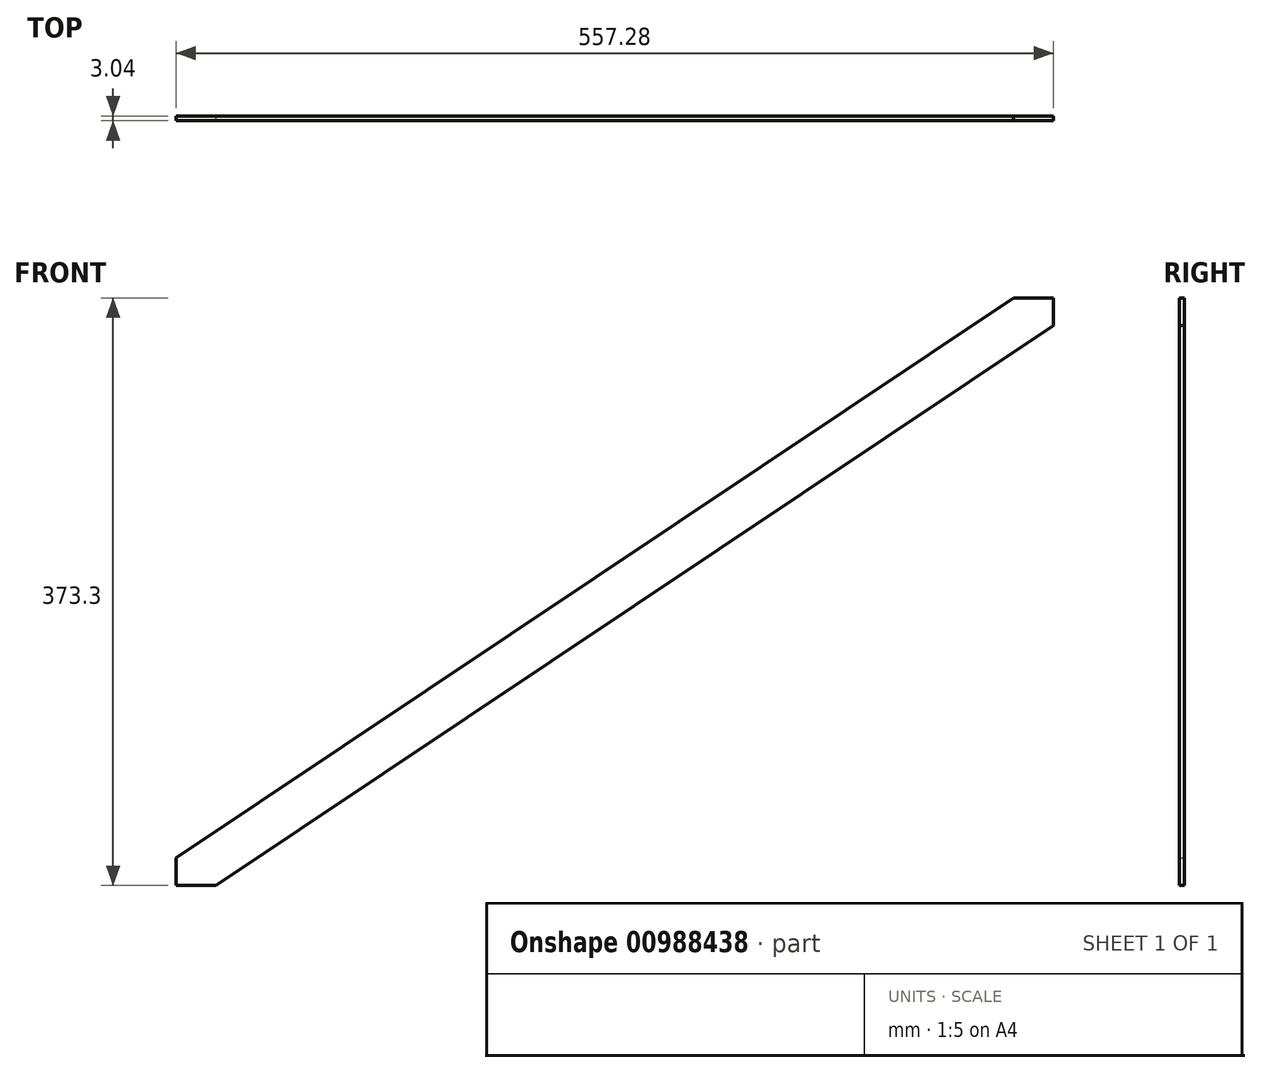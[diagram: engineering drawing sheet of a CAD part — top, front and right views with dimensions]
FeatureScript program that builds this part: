
annotation { "Feature Type Name" : "Feature", "Feature Type Description" : "" }
export const myFeature = defineFeature(function(context is Context, id is Id, definition is map)
    precondition{}
    {
        {
            var Q0;
            Q0=qCreatedBy(makeId("Front.planeOp"),FACE);
            var sketch = newSketch(context, id + "F0", { "sketchPlane" : qUnion([Q0])});
            skLineSegment(sketch, "E0.bottom", {"start": v(278.64, 186.65) * mm, "end": v(-278.64, 186.65) * mm, "construction": true});
            skLineSegment(sketch, "E0.top", {"start": v(278.64, -186.65) * mm, "end": v(-278.64, -186.65) * mm, "construction": true});
            skLineSegment(sketch, "E0.left", {"start": v(278.64, 186.65) * mm, "end": v(278.64, -186.65) * mm, "construction": true});
            skLineSegment(sketch, "E0.right", {"start": v(-278.64, 186.65) * mm, "end": v(-278.64, -186.65) * mm, "construction": true});
            skPoint(sketch, "E0.middle", {"position": v(0, 0) * mm});
            skSolve(sketch);
        }
        {
            var Q0;
            Q0=qCreatedBy(makeId("Front.planeOp"),FACE);
            var sketch = newSketch(context, id + "F1", { "sketchPlane" : qUnion([Q0])});
            skLineSegment(sketch, "E1", {"start": v(278.64, 186.65) * mm, "end": v(253.24, 186.65) * mm});
            skLineSegment(sketch, "E2", {"start": v(253.24, 186.65) * mm, "end": v(-278.64, -169.05) * mm});
            skLineSegment(sketch, "E3", {"start": v(-278.64, -169.05) * mm, "end": v(-278.64, -186.65) * mm});
            skLineSegment(sketch, "E4", {"start": v(-278.64, -186.65) * mm, "end": v(-253.24, -186.65) * mm});
            skLineSegment(sketch, "E5", {"start": v(-253.24, -186.65) * mm, "end": v(278.64, 169.05) * mm});
            skLineSegment(sketch, "E6", {"start": v(278.64, 169.05) * mm, "end": v(278.64, 186.65) * mm});
            skSolve(sketch);
        }
        {
            var Q0;
            Q0 = qSketchRegion(id + "F1", true);
            extrude(context, id + "F2", {"entities" : qUnion([Q0]), "depth" : 3.04 * mm, "offsetDistance" : 25.4 * mm, "symmetric" : true});
        }
    });
